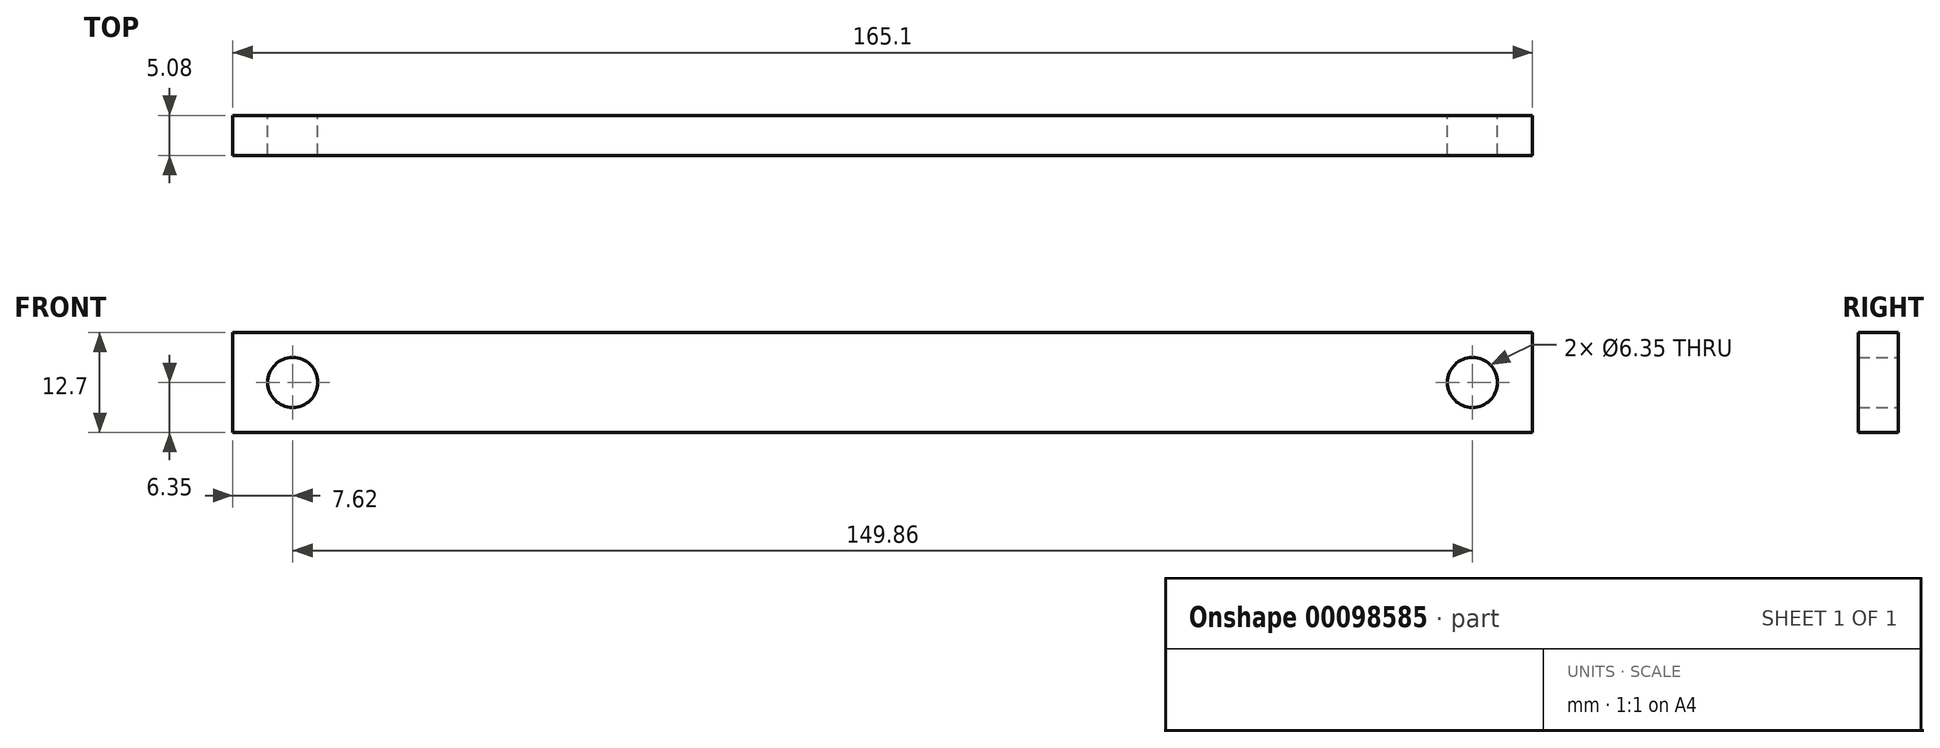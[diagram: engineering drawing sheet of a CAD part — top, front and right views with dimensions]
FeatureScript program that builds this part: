
annotation { "Feature Type Name" : "Feature", "Feature Type Description" : "" }
export const myFeature = defineFeature(function(context is Context, id is Id, definition is map)
    precondition{}
    {
        {
            var Q0;
            Q0=qCreatedBy(makeId("Front.planeOp"),FACE);
            var sketch = newSketch(context, id + "F0", { "sketchPlane" : qUnion([Q0])});
            skLineSegment(sketch, "E0.bottom", {"start": v(-82.55, 6.35) * mm, "end": v(82.55, 6.35) * mm});
            skLineSegment(sketch, "E0.top", {"start": v(-82.55, -6.35) * mm, "end": v(82.55, -6.35) * mm});
            skLineSegment(sketch, "E0.left", {"start": v(-82.55, 6.35) * mm, "end": v(-82.55, -6.35) * mm});
            skLineSegment(sketch, "E0.right", {"start": v(82.55, 6.35) * mm, "end": v(82.55, -6.35) * mm});
            skCircle(sketch, "E1", {"center": v(-74.93, 0) * mm, "radius": 3.18 * mm});
            skCircle(sketch, "E2", {"center": v(74.93, 0) * mm, "radius": 3.18 * mm});
            skSolve(sketch);
        }
        {
            var Q0;
            Q0 = qSketchRegion(id + "F0", true);
            var Q1;
            Q1=makeQuery(id+"F0.imprint","IMPRINT",FACE,{"disambiguationData":[TD([[makeQuery(id+"F0.imprint","IMPRINT",EDGE,{"derivedFrom":sQuery(id+"F0.wireOp",EDGE,"E0.bottom")}),-1.0]])]});
            extrude(context, id + "F1", {"entities" : qUnion([Q0, Q1]), "depth" : 5.08 * mm});
        }
    });
